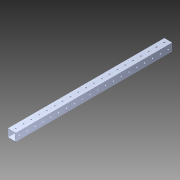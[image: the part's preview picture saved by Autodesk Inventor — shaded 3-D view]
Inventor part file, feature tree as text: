
AUTODESK INVENTOR PART (.ipt)
format: ipt  version: 2014 SP1 (Build 180222100, 222)  size: 1,201,664 bytes
history: native  units: in
note: dims shown in document units (in); Inventor stores cm internally (conversion verified against a paired STEP export)
features: pattern_circular x1, other x1, extrude x1, imported_body x1, sketch x1
ambient origin geometry x8: Origin, YZ Plane, XZ Plane, XY Plane, X Axis, Y Axis, Z Axis, Center Point
bodies: Body1 (feature_tree)
feature tree (5):
  pattern_circular  "CirPattern2"
  other  "1x1 tube1"
  extrude  "Extrusion1"  [1 undecoded]
  imported_body  "Base1"
  sketch  "Sketch1"  dims[d0=39.0in d1=0.0in]
note: 1 required parameter value undecoded (feature->parameter linkage not recoverable at this tier; creation-order binding heuristic only, values carry confidence <= 0.55)
